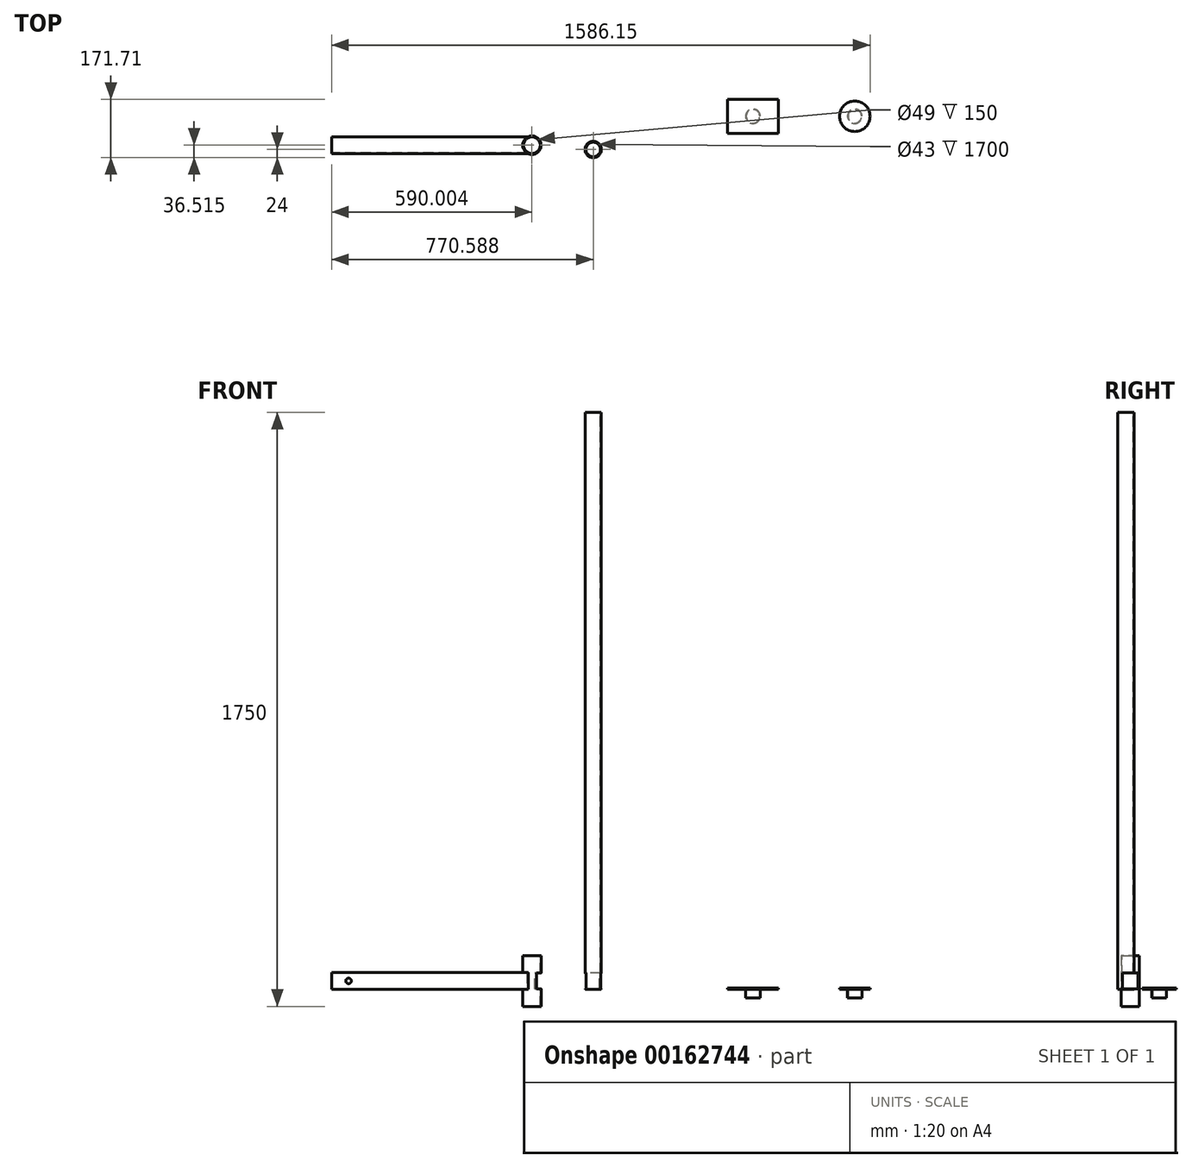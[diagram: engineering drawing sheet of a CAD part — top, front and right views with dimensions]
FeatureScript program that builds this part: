
annotation { "Feature Type Name" : "Feature", "Feature Type Description" : "" }
export const myFeature = defineFeature(function(context is Context, id is Id, definition is map)
    precondition{}
    {
        {
            var Q0;
            Q0=qCreatedBy(makeId("Top.planeOp"),FACE);
            var sketch = newSketch(context, id + "F0", { "sketchPlane" : qUnion([Q0])});
            skLineSegment(sketch, "E0", {"start": v(-79.6, 37.52) * mm, "end": v(535.4, 37.52) * mm});
            skLineSegment(sketch, "E1", {"start": v(-79.6, 37.52) * mm, "end": v(-79.6, -12.48) * mm});
            skLineSegment(sketch, "E2", {"start": v(-79.6, -12.48) * mm, "end": v(535.4, -12.48) * mm});
            skLineSegment(sketch, "E3", {"start": v(535.4, -12.48) * mm, "end": v(535.4, 37.52) * mm});
            skCircle(sketch, "E4", {"center": v(510.4, 12.52) * mm, "radius": 27 * mm});
            skPoint(sketch, "E4.centerSnap0", {"position": v(535.4, 12.52) * mm});
            skLineSegment(sketch, "E5", {"start": v(510.4, 12.52) * mm, "end": v(535.4, 12.52) * mm, "construction": true});
            skSolve(sketch);
        }
        {
            var Q0;
            {var subQ0=sQuery(id+"F0.wireOp",EDGE,"E1");Q0=makeQuery(id+"F0.imprint","IMPRINT",FACE,{"disambiguationData":[TD([[makeQuery(id+"F0.imprint","IMPRINT",EDGE,{"derivedFrom":subQ0}),1.0]])]});}
            extrude(context, id + "F1", {"entities" : qUnion([Q0]), "depth" : 50 * mm});
        }
        {
            var Q0;
            Q0=makeQuery(id+"F1.opExtrude","SWEPT_FACE",FACE,{"disambiguationData":[OSD([sQuery(id+"F0.wireOp",EDGE,"E2")])]});
            var sketch = newSketch(context, id + "F2", { "sketchPlane" : qUnion([Q0])});
            skLineSegment(sketch, "E6", {"start": v(-79.6, 25) * mm, "end": v(-29.6, 25) * mm, "construction": true});
            skCircle(sketch, "E7", {"center": v(-29.6, 25) * mm, "radius": 8.15 * mm});
            skSolve(sketch);
        }
        {
            var Q0;
            Q0=makeQuery(id+"F2.imprint","IMPRINT",FACE,{"disambiguationData":[TD([[makeQuery(id+"F2.imprint","IMPRINT",EDGE,{"derivedFrom":sQuery(id+"F2.wireOp",EDGE,"E7")}),1.0]])]});
            extrude(context, id + "F3", {"entities" : qUnion([Q0]), "operationType" : NewBodyOperationType.REMOVE, "endBound" : BoundingType.THROUGH_ALL, "oppositeDirection" : true, "depth" : 25 * mm});
        }
        {
            var Q0;
            {var subQ0=sQuery(id+"F0.wireOp",EDGE,"E4");var subQ1=sQuery(id+"F0.wireOp",EDGE,"E0");var subQ6=makeQuery(id+"F0.imprint","INTERSECT",VERTEX,{"disambiguationData":[OD(0.0)],"derivedFrom":[subQ1,subQ0]});Q0=makeQuery(id+"F0.imprint","IMPRINT",FACE,{"disambiguationData":[TD([[makeQuery(id+"F0.imprint","IMPRINT",EDGE,{"disambiguationData":[TD([[subQ6,-1.0]])],"derivedFrom":subQ1}),-1.0]])]});}
            var Q1;
            {var subQ0=sQuery(id+"F0.wireOp",EDGE,"E4");var subQ1=sQuery(id+"F0.wireOp",EDGE,"E2");var subQ2=makeQuery(id+"F0.imprint","INTERSECT",VERTEX,{"disambiguationData":[OD(0.0)],"derivedFrom":[subQ1,subQ0]});Q1=makeQuery(id+"F0.imprint","IMPRINT",FACE,{"disambiguationData":[TD([[makeQuery(id+"F0.imprint","IMPRINT",EDGE,{"disambiguationData":[TD([[subQ2,-1.0]])],"derivedFrom":subQ1}),-1.0]])]});}
            var Q2;
            {var subQ0=sQuery(id+"F0.wireOp",EDGE,"E4");var subQ1=sQuery(id+"F0.wireOp",EDGE,"E3");var subQ2=makeQuery(id+"F0.imprint","INTERSECT",VERTEX,{"disambiguationData":[OD(0.0)],"derivedFrom":[subQ1,subQ0]});Q2=makeQuery(id+"F0.imprint","IMPRINT",FACE,{"disambiguationData":[TD([[makeQuery(id+"F0.imprint","IMPRINT",EDGE,{"disambiguationData":[TD([[subQ2,-1.0]])],"derivedFrom":subQ1}),-1.0]])]});}
            var Q3;
            {var subQ0=sQuery(id+"F0.wireOp",EDGE,"E4");var subQ1=sQuery(id+"F0.wireOp",EDGE,"E0");var subQ2=makeQuery(id+"F0.imprint","INTERSECT",VERTEX,{"disambiguationData":[OD(0.0)],"derivedFrom":[subQ1,subQ0]});Q3=makeQuery(id+"F0.imprint","IMPRINT",FACE,{"disambiguationData":[TD([[makeQuery(id+"F0.imprint","IMPRINT",EDGE,{"disambiguationData":[TD([[subQ2,-1.0]])],"derivedFrom":subQ1}),1.0]])]});}
            extrude(context, id + "F4", {"entities" : qUnion([Q0, Q1, Q2, Q3]), "depth" : 100 * mm, "hasSecondDirection" : true, "secondDirectionOppositeDirection" : true, "secondDirectionDepth" : 50 * mm});
        }
        {
            var Q0;
            Q0=makeQuery(id+"F4.opExtrude","CAP_FACE",FACE,{"disambiguationData":[OSD([sQuery(id+"F0.wireOp",EDGE,"E4")])],"isStart":false});
            var sketch = newSketch(context, id + "F5", { "sketchPlane" : qUnion([Q0])});
            skCircle(sketch, "E8", {"center": v(510.4, 12.52) * mm, "radius": 24.5 * mm});
            skSolve(sketch);
        }
        {
            var Q0;
            Q0=makeQuery(id+"F5.imprint","IMPRINT",FACE,{"disambiguationData":[TD([[makeQuery(id+"F5.imprint","IMPRINT",EDGE,{"derivedFrom":sQuery(id+"F5.wireOp",EDGE,"E8")}),1.0]])]});
            extrude(context, id + "F6", {"entities" : qUnion([Q0]), "operationType" : NewBodyOperationType.REMOVE, "endBound" : BoundingType.THROUGH_ALL, "oppositeDirection" : true, "depth" : 25 * mm});
        }
        {
            var Q0;
            Q0=qCreatedBy(makeId("Top.planeOp"),FACE);
            var sketch = newSketch(context, id + "F7", { "sketchPlane" : qUnion([Q0])});
            skCircle(sketch, "E9", {"center": v(690.99, 0) * mm, "radius": 24 * mm});
            skSolve(sketch);
        }
        {
            var Q0;
            Q0=makeQuery(id+"F7.imprint","IMPRINT",FACE,{"disambiguationData":[TD([[makeQuery(id+"F7.imprint","IMPRINT",EDGE,{"derivedFrom":sQuery(id+"F7.wireOp",EDGE,"E9")}),1.0]])]});
            extrude(context, id + "F8", {"entities" : qUnion([Q0]), "depth" : 1700 * mm});
        }
        {
            var Q0;
            Q0=makeQuery(id+"F8.opExtrude","CAP_FACE",FACE,{"disambiguationData":[OSD([sQuery(id+"F7.wireOp",EDGE,"E9")])],"isStart":false});
            var sketch = newSketch(context, id + "F9", { "sketchPlane" : qUnion([Q0])});
            skCircle(sketch, "E10", {"center": v(690.99, 0) * mm, "radius": 21.5 * mm});
            skSolve(sketch);
        }
        {
            var Q0;
            Q0=makeQuery(id+"F9.imprint","IMPRINT",FACE,{"disambiguationData":[TD([[makeQuery(id+"F9.imprint","IMPRINT",EDGE,{"derivedFrom":sQuery(id+"F9.wireOp",EDGE,"E10")}),1.0]])]});
            extrude(context, id + "F10", {"entities" : qUnion([Q0]), "operationType" : NewBodyOperationType.REMOVE, "endBound" : BoundingType.THROUGH_ALL, "oppositeDirection" : true, "depth" : 25 * mm});
        }
        {
            var Q0;
            Q0=qCreatedBy(makeId("Top.planeOp"),FACE);
            var sketch = newSketch(context, id + "F11", { "sketchPlane" : qUnion([Q0])});
            skLineSegment(sketch, "E11.bottom", {"start": v(1086.55, 147.71) * mm, "end": v(1236.55, 147.71) * mm});
            skLineSegment(sketch, "E11.top", {"start": v(1086.55, 47.71) * mm, "end": v(1236.55, 47.71) * mm});
            skLineSegment(sketch, "E11.left", {"start": v(1086.55, 147.71) * mm, "end": v(1086.55, 47.71) * mm});
            skLineSegment(sketch, "E11.right", {"start": v(1236.55, 147.71) * mm, "end": v(1236.55, 47.71) * mm});
            skLineSegment(sketch, "E12", {"start": v(1161.55, 47.71) * mm, "end": v(1161.55, 147.71) * mm, "construction": true});
            skCircle(sketch, "E13", {"center": v(1161.55, 97.71) * mm, "radius": 21.5 * mm});
            skSolve(sketch);
        }
        {
            var Q0;
            Q0 = qSketchRegion(id + "F11", true);
            var Q1;
            Q1=makeQuery(id+"F11.imprint","IMPRINT",FACE,{"disambiguationData":[TD([[makeQuery(id+"F11.imprint","IMPRINT",EDGE,{"derivedFrom":sQuery(id+"F11.wireOp",EDGE,"E13")}),1.0]])]});
            extrude(context, id + "F12", {"entities" : qUnion([Q0, Q1]), "depth" : 4 * mm});
        }
        {
            var Q0;
            Q0=makeQuery(id+"F11.imprint","IMPRINT",FACE,{"disambiguationData":[TD([[makeQuery(id+"F11.imprint","IMPRINT",EDGE,{"derivedFrom":sQuery(id+"F11.wireOp",EDGE,"E13")}),1.0]])]});
            extrude(context, id + "F13", {"entities" : qUnion([Q0]), "operationType" : NewBodyOperationType.ADD, "oppositeDirection" : true, "depth" : 25 * mm});
        }
        {
            var Q0;
            Q0=makeQuery(id+"F13.opExtrude","CAP_FACE",FACE,{"disambiguationData":[OSD([sQuery(id+"F11.wireOp",EDGE,"E13")])],"isStart":false});
            var sketch = newSketch(context, id + "F14", { "sketchPlane" : qUnion([Q0])});
            skCircle(sketch, "E14", {"center": v(1161.55, -97.71) * mm, "radius": 20 * mm});
            skSolve(sketch);
        }
        {
            var Q0;
            Q0=makeQuery(id+"F14.imprint","IMPRINT",FACE,{"disambiguationData":[TD([[makeQuery(id+"F14.imprint","IMPRINT",EDGE,{"derivedFrom":sQuery(id+"F14.wireOp",EDGE,"E14")}),1.0]])]});
            extrude(context, id + "F15", {"entities" : qUnion([Q0]), "operationType" : NewBodyOperationType.REMOVE, "oppositeDirection" : true, "depth" : 25 * mm});
        }
        {
            var Q0;
            Q0=makeQuery(id+"F12.opExtrude","SWEPT_BODY",BODY,{"disambiguationData":[OSD([sQuery(id+"F11.wireOp",EDGE,"E11.bottom"),sQuery(id+"F11.wireOp",EDGE,"E11.top"),sQuery(id+"F11.wireOp",EDGE,"E11.left"),sQuery(id+"F11.wireOp",EDGE,"E11.right")])]});
            transform(context, id + "F16", {"entities" : qUnion([Q0]), "transformType" : TransformType.TRANSLATION_3D, "dx" : 300 * mm, "dy" : 0 * mm, "dz" : 0 * mm, "makeCopy" : true});
        }
        {
            var Q0;
            Q0=makeQuery(id+"F16.opPattern","COPY",FACE,{"derivedFrom":makeQuery(id+"F12.opExtrude","CAP_FACE",FACE,{"disambiguationData":[OSD([sQuery(id+"F11.wireOp",EDGE,"E11.bottom"),sQuery(id+"F11.wireOp",EDGE,"E11.top"),sQuery(id+"F11.wireOp",EDGE,"E11.left"),sQuery(id+"F11.wireOp",EDGE,"E11.right")])],"isStart":false}),"instanceName":"1"});
            var sketch = newSketch(context, id + "F17", { "sketchPlane" : qUnion([Q0])});
            skLineSegment(sketch, "E15", {"start": v(1461.55, 47.71) * mm, "end": v(1461.55, 147.71) * mm, "construction": true});
            skCircle(sketch, "E16", {"center": v(1461.55, 97.71) * mm, "radius": 45 * mm});
            skSolve(sketch);
        }
        {
            var Q0;
            Q0=makeQuery(id+"F17.imprint","IMPRINT",FACE,{"disambiguationData":[TD([[makeQuery(id+"F17.imprint","IMPRINT",EDGE,{"derivedFrom":sQuery(id+"F17.wireOp",EDGE,"E16")}),-1.0]])]});
            extrude(context, id + "F18", {"entities" : qUnion([Q0]), "operationType" : NewBodyOperationType.REMOVE, "endBound" : BoundingType.THROUGH_ALL, "oppositeDirection" : true, "depth" : 25 * mm});
        }
        {
            var Q0;
            Q0=makeQuery(id+"F1.opExtrude","SWEPT_FACE",FACE,{"disambiguationData":[OSD([sQuery(id+"F0.wireOp",EDGE,"E1")])]});
            var sketch = newSketch(context, id + "F19", { "sketchPlane" : qUnion([Q0])});
            skLineSegment(sketch, "E17.0", {"start": v(-35.52, 2) * mm, "end": v(10.48, 2) * mm});
            skLineSegment(sketch, "E17.1", {"start": v(-35.52, 48) * mm, "end": v(-35.52, 2) * mm});
            skLineSegment(sketch, "E17.2", {"start": v(10.48, 48) * mm, "end": v(-35.52, 48) * mm});
            skLineSegment(sketch, "E17.3", {"start": v(10.48, 2) * mm, "end": v(10.48, 48) * mm});
            skSolve(sketch);
        }
        {
            var Q0;
            Q0=makeQuery(id+"F19.imprint","IMPRINT",FACE,{"disambiguationData":[TD([[makeQuery(id+"F19.imprint","IMPRINT",EDGE,{"derivedFrom":sQuery(id+"F19.wireOp",EDGE,"E17.0")}),1.0]])]});
            extrude(context, id + "F20", {"entities" : qUnion([Q0]), "operationType" : NewBodyOperationType.REMOVE, "endBound" : BoundingType.THROUGH_ALL, "oppositeDirection" : true, "depth" : 25 * mm});
        }
        {
            var Q0;
            Q0=makeQuery(id+"F5.imprint","IMPRINT",FACE,{"disambiguationData":[TD([[makeQuery(id+"F5.imprint","IMPRINT",EDGE,{"derivedFrom":sQuery(id+"F5.wireOp",EDGE,"E8")}),1.0]])]});
            extrude(context, id + "F21", {"entities" : qUnion([Q0]), "operationType" : NewBodyOperationType.REMOVE, "endBound" : BoundingType.THROUGH_ALL, "oppositeDirection" : true, "depth" : 25 * mm});
        }
    });
